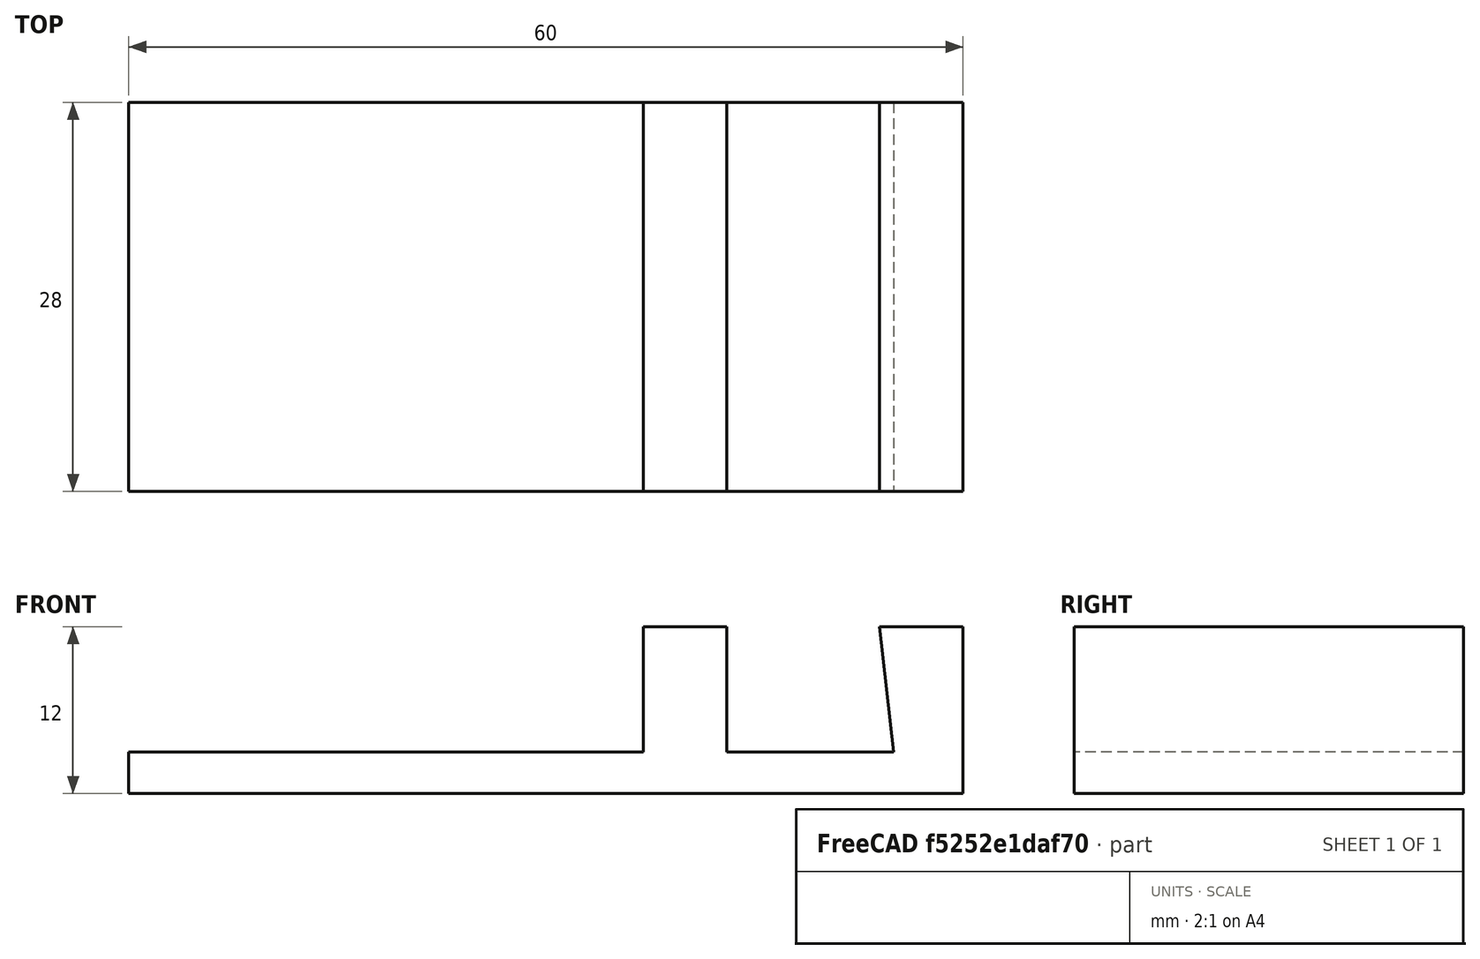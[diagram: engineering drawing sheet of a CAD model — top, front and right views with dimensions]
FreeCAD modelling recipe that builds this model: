
FCSTD DOCUMENT  (FreeCAD 0.17R13217 (Git))
Label: 03-soporte-movil
License: All rights reserved
LicenseURL: http://en.wikipedia.org/wiki/All_rights_reserved
objects: Sketcher::SketchObject×1, PartDesign::Pad×1, PartDesign::Body×1
note: 4 computed .brp shape members not serialized (recipe doc carries the construction recipe); baked Part::Feature solids carry a one-line shape summary decoded from their .brp

FEATURE [Sketcher::SketchObject] Sketch
  MapMode = 5
  Placement = pos=(0,0,0) rot=(1,0,0;1.5708rad)
  Support = -> [XZ_Plane]
  sketch-geometry (10):
    g0: LineSegment StartX=0 StartY=0 StartZ=0 EndX=0 EndY=3 EndZ=0
    g1: LineSegment StartX=43 StartY=12 StartZ=0 EndX=43 EndY=3 EndZ=0
    g2: LineSegment StartX=43 StartY=3 StartZ=0 EndX=55 EndY=3 EndZ=0
    g3: LineSegment StartX=55 StartY=3 StartZ=0 EndX=54 EndY=12 EndZ=0
    g4: LineSegment StartX=54 StartY=12 StartZ=0 EndX=60 EndY=12 EndZ=0
    g5: LineSegment StartX=60 StartY=12 StartZ=0 EndX=60 EndY=0 EndZ=0
    g6: LineSegment StartX=60 StartY=0 StartZ=0 EndX=0 EndY=0 EndZ=0
    g7: LineSegment StartX=0 StartY=3 StartZ=0 EndX=37 EndY=3 EndZ=0
    g8: LineSegment StartX=37 StartY=3 StartZ=0 EndX=37 EndY=12 EndZ=0
    g9: LineSegment StartX=37 StartY=12 StartZ=0 EndX=43 EndY=12 EndZ=0
  constraints (29):
    c: Vertical(g0)
    c: Coincident(g1,g2)
    c: Horizontal(g2)
    c: Coincident(g2,g3)
    c: Coincident(g3,g4)
    c: Horizontal(g4)
    c: Coincident(g4,g5)
    c: Vertical(g5)
    c: Coincident(g5,g6)
    c: Coincident(g6,g0)
    c: Horizontal(g6)
    c: Coincident(g0,g7)
    c: Horizontal(g7)
    c: Coincident(g7,g8)
    c: Coincident(g8,g9)
    c: Coincident(g9,g1)
    c: Vertical(g8)
    c: Horizontal(g9)
    c: Vertical(g1)
    c: DistanceY(g0,g0) = 3
    c: DistanceX(g1,g3) = 11
    c: DistanceY(g0,g8) = 12
    c: PointOnObject(g7,g2)
    c: DistanceX(g2,g2) = 12
    c: DistanceX(g4,g4) = 6
    c: Equal(g4,g9)
    c: DistanceX(g6,g6) = 60
    c: PointOnObject(g1,g4)
    c: Coincident(g0,g-1)
FEATURE [PartDesign::Pad] Pad
  Length = 28
  Length2 = 100
  Placement = pos=(0,0,0) rot=(1,0,0;1.5708rad)
  Profile = -> Sketch
  Refine = true
  Type = 0
FEATURE [PartDesign::Body] Body
  Group = -> [Sketch,Pad]
  Origin = -> Origin
  Tip = -> Pad
